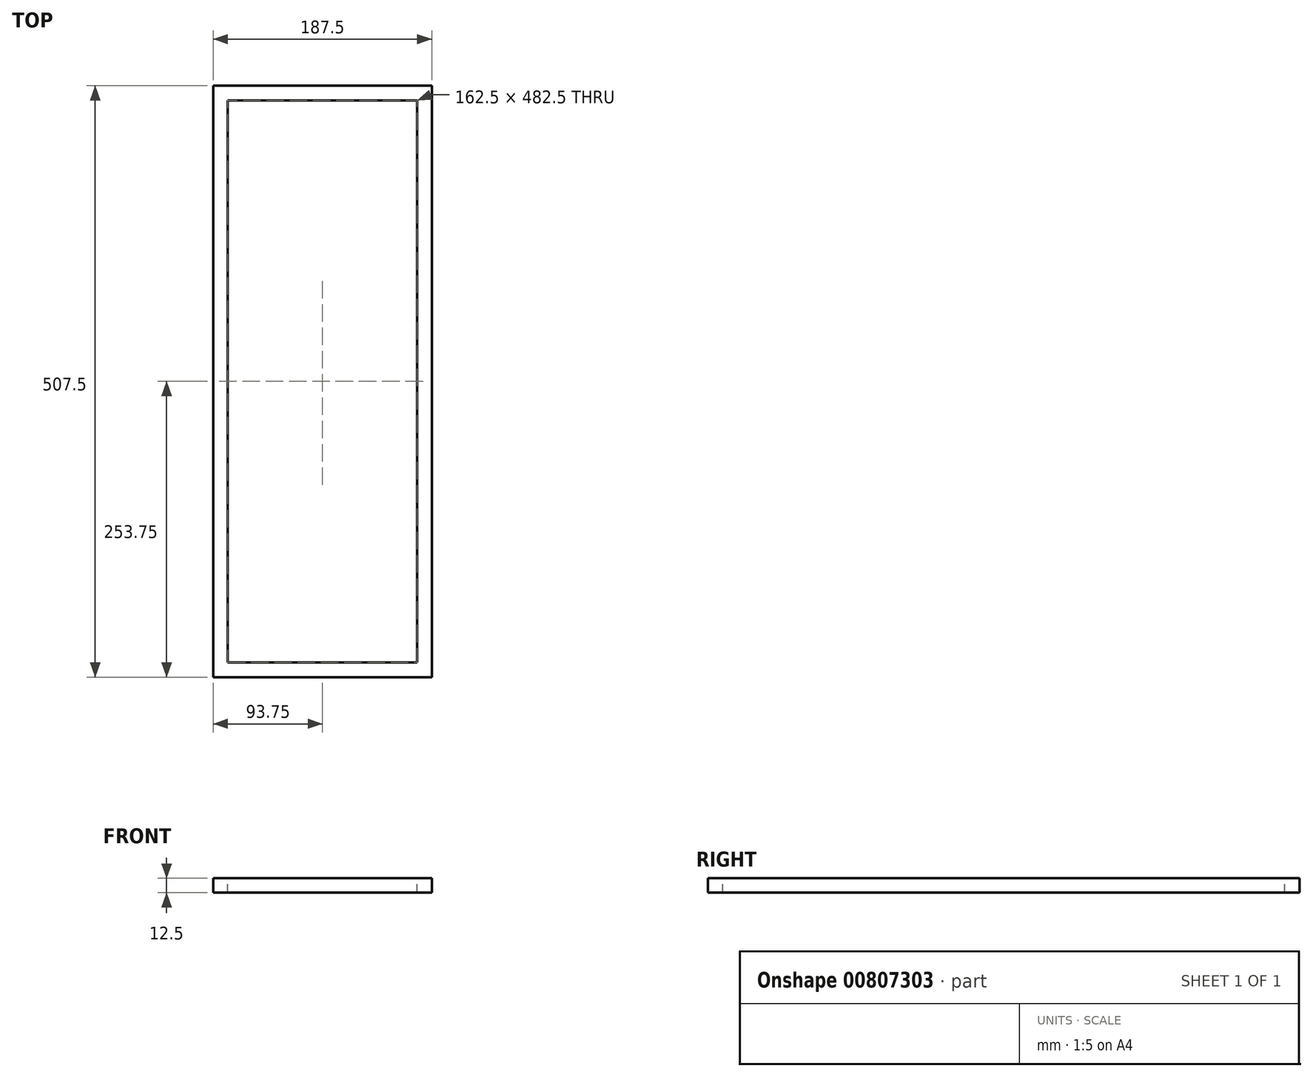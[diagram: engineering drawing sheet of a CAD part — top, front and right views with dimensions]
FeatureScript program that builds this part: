
annotation { "Feature Type Name" : "Feature", "Feature Type Description" : "" }
export const myFeature = defineFeature(function(context is Context, id is Id, definition is map)
    precondition{}
    {
        {
            var Q0;
            Q0=qCreatedBy(makeId("Top.planeOp"),FACE);
            var sketch = newSketch(context, id + "F0", { "sketchPlane" : qUnion([Q0])});
            skLineSegment(sketch, "E0", {"start": v(0, 0) * mm, "end": v(0, 495) * mm});
            skLineSegment(sketch, "E1", {"start": v(0, 495) * mm, "end": v(175, 495) * mm});
            skLineSegment(sketch, "E2", {"start": v(175, 495) * mm, "end": v(175, 0) * mm});
            skLineSegment(sketch, "E3", {"start": v(175, 0) * mm, "end": v(0, 0) * mm});
            skSolve(sketch);
        }
        {
            var Q0;
            Q0=qCreatedBy(makeId("Front.planeOp"),FACE);
            var sketch = newSketch(context, id + "F1", { "sketchPlane" : qUnion([Q0])});
            skLineSegment(sketch, "E4.bottom", {"start": v(6.25, 6.25) * mm, "end": v(-6.25, 6.25) * mm});
            skLineSegment(sketch, "E4.top", {"start": v(6.25, -6.25) * mm, "end": v(-6.25, -6.25) * mm});
            skLineSegment(sketch, "E4.left", {"start": v(6.25, 6.25) * mm, "end": v(6.25, -6.25) * mm});
            skLineSegment(sketch, "E4.right", {"start": v(-6.25, 6.25) * mm, "end": v(-6.25, -6.25) * mm});
            skPoint(sketch, "E4.middle", {"position": v(0, 0) * mm});
            skSolve(sketch);
        }
        {
            var Q0;
            Q0=makeQuery(id+"F1.imprint","IMPRINT",FACE,{"disambiguationData":[TD([[makeQuery(id+"F1.imprint","IMPRINT",EDGE,{"derivedFrom":sQuery(id+"F1.wireOp",EDGE,"E4.bottom")}),1.0]])]});
            var Q1;
            Q1=sQuery(id+"F0.wireOp",EDGE,"E0");
            var Q2;
            Q2=sQuery(id+"F0.wireOp",EDGE,"E1");
            var Q3;
            Q3=sQuery(id+"F0.wireOp",EDGE,"E2");
            var Q4;
            Q4=sQuery(id+"F0.wireOp",EDGE,"E3");
            sweep(context, id + "F2", {"profiles" : qUnion([Q0]), "path" : qUnion([Q1, Q2, Q3, Q4])});
        }
    });
